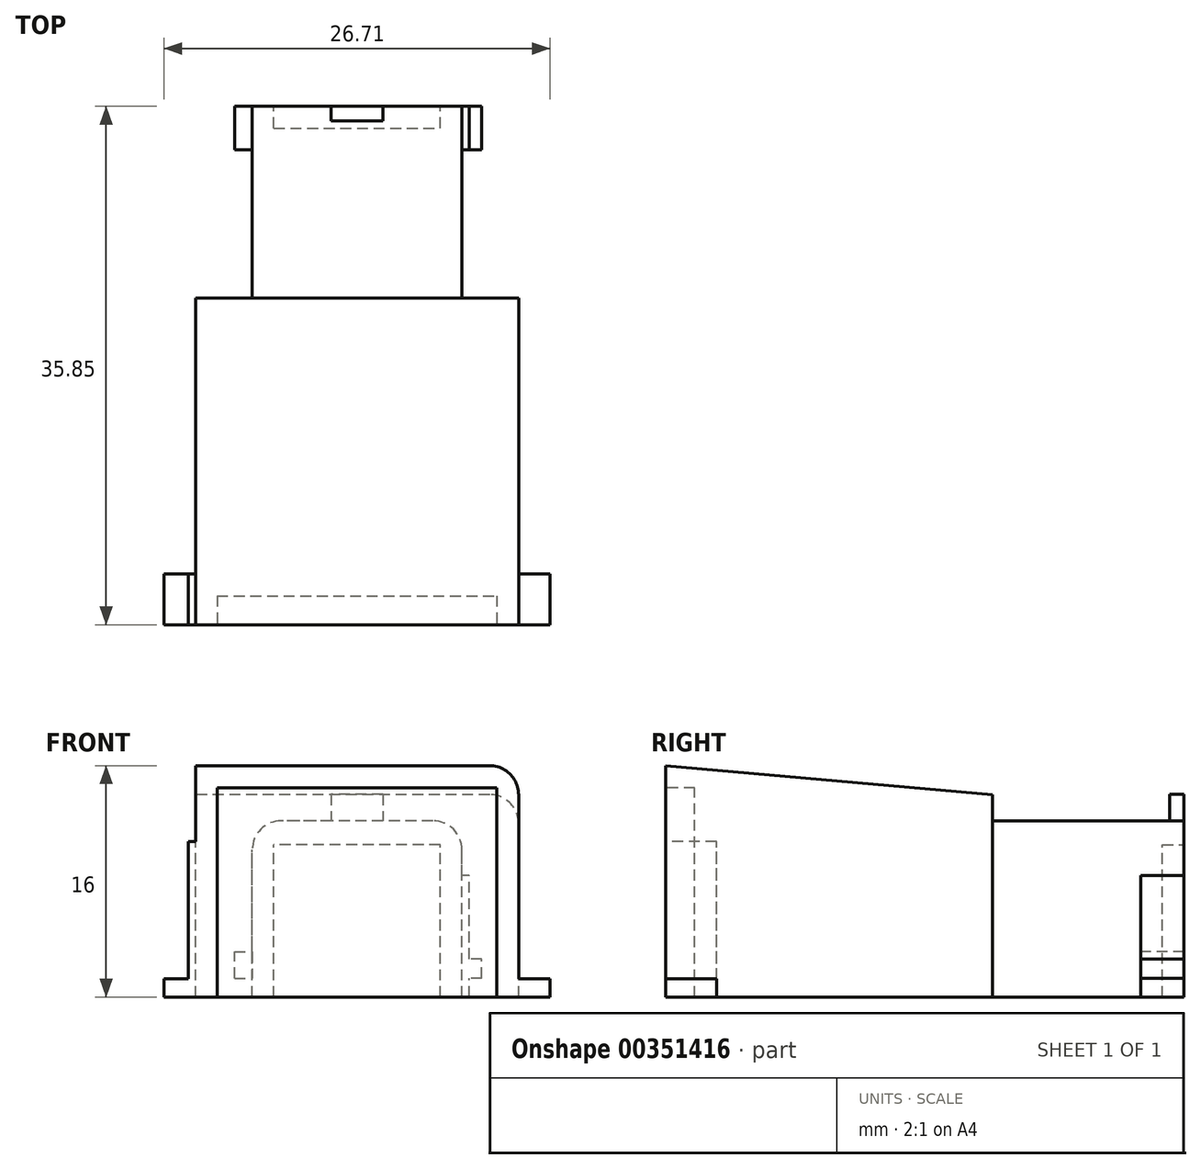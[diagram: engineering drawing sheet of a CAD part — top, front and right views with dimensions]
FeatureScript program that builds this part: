
annotation { "Feature Type Name" : "Feature", "Feature Type Description" : "" }
export const myFeature = defineFeature(function(context is Context, id is Id, definition is map)
    precondition{}
    {
        {
            var Q0;
            Q0=qCreatedBy(makeId("Front.planeOp"),FACE);
            var sketch = newSketch(context, id + "F0", { "sketchPlane" : qUnion([Q0])});
            skLineSegment(sketch, "E0.bottom", {"start": v(-13.6, 0) * mm, "end": v(8.76, 0) * mm});
            skLineSegment(sketch, "E0.top", {"start": v(-13.6, 16) * mm, "end": v(8.76, 16) * mm});
            skLineSegment(sketch, "E0.left", {"start": v(-13.6, 0) * mm, "end": v(-13.6, 16) * mm});
            skLineSegment(sketch, "E0.right", {"start": v(8.76, 0) * mm, "end": v(8.76, 16) * mm});
            skSolve(sketch);
        }
        {
            var Q0;
            Q0 = qSketchRegion(id + "F0", true);
            extrude(context, id + "F1", {"entities" : qUnion([Q0]), "depth" : 22.6 * mm});
        }
        {
            var Q0;
            Q0=makeQuery(id+"F1.opExtrude","CAP_FACE",FACE,{"disambiguationData":[OSD([sQuery(id+"F0.wireOp",EDGE,"E0.bottom"),sQuery(id+"F0.wireOp",EDGE,"E0.top"),sQuery(id+"F0.wireOp",EDGE,"E0.left"),sQuery(id+"F0.wireOp",EDGE,"E0.right")])],"isStart":false});
            var sketch = newSketch(context, id + "F2", { "sketchPlane" : qUnion([Q0])});
            skLineSegment(sketch, "E1.bottom", {"start": v(-12.1, 0) * mm, "end": v(7.26, 0) * mm});
            skLineSegment(sketch, "E1.top", {"start": v(-12.1, 14.48) * mm, "end": v(7.26, 14.48) * mm});
            skLineSegment(sketch, "E1.left", {"start": v(-12.1, 0) * mm, "end": v(-12.1, 14.48) * mm});
            skLineSegment(sketch, "E1.right", {"start": v(7.26, 0) * mm, "end": v(7.26, 14.48) * mm});
            skSolve(sketch);
        }
        {
            var Q0;
            Q0 = qSketchRegion(id + "F2", true);
            extrude(context, id + "F3", {"entities" : qUnion([Q0]), "operationType" : NewBodyOperationType.REMOVE, "oppositeDirection" : true, "depth" : 2 * mm});
        }
        {
            var Q0;
            Q0=makeQuery(id+"F1.opExtrude","SWEPT_FACE",FACE,{"disambiguationData":[OSD([sQuery(id+"F0.wireOp",EDGE,"E0.left")])]});
            var sketch = newSketch(context, id + "F4", { "sketchPlane" : qUnion([Q0])});
            skLineSegment(sketch, "E2", {"start": v(0, 0) * mm, "end": v(0, 14) * mm, "construction": true});
            skLineSegment(sketch, "E3", {"start": v(0, 14) * mm, "end": v(22.6, 16) * mm});
            skLineSegment(sketch, "E4", {"start": v(22.6, 16) * mm, "end": v(0, 16) * mm});
            skLineSegment(sketch, "E5", {"start": v(0, 16) * mm, "end": v(0, 14) * mm});
            skSolve(sketch);
        }
        {
            var Q0;
            Q0 = qSketchRegion(id + "F4", true);
            extrude(context, id + "F5", {"entities" : qUnion([Q0]), "operationType" : NewBodyOperationType.REMOVE, "oppositeDirection" : true, "depth" : 25 * mm});
        }
        {
            var Q0;
            Q0=makeQuery(id+"F1.opExtrude","SWEPT_FACE",FACE,{"disambiguationData":[OSD([sQuery(id+"F0.wireOp",EDGE,"E0.left")])]});
            var sketch = newSketch(context, id + "F6", { "sketchPlane" : qUnion([Q0])});
            skLineSegment(sketch, "E6.bottom", {"start": v(22.6, 0) * mm, "end": v(19.1, 0) * mm});
            skLineSegment(sketch, "E6.top", {"start": v(22.6, 1.25) * mm, "end": v(19.1, 1.25) * mm});
            skLineSegment(sketch, "E6.left", {"start": v(22.6, 0) * mm, "end": v(22.6, 1.25) * mm});
            skLineSegment(sketch, "E6.right", {"start": v(19.1, 0) * mm, "end": v(19.1, 1.25) * mm});
            skSolve(sketch);
        }
        {
            var Q0;
            Q0 = qSketchRegion(id + "F6", true);
            extrude(context, id + "F7", {"entities" : qUnion([Q0]), "operationType" : NewBodyOperationType.ADD, "depth" : 2.18 * mm});
        }
        {
            var Q0;
            Q0=makeQuery(id+"F1.opExtrude","SWEPT_FACE",FACE,{"disambiguationData":[OSD([sQuery(id+"F0.wireOp",EDGE,"E0.right")])]});
            var sketch = newSketch(context, id + "F8", { "sketchPlane" : qUnion([Q0])});
            skLineSegment(sketch, "E7.bottom", {"start": v(-22.6, 0) * mm, "end": v(-19.1, 0) * mm});
            skLineSegment(sketch, "E7.top", {"start": v(-22.6, 1.25) * mm, "end": v(-19.1, 1.25) * mm});
            skLineSegment(sketch, "E7.left", {"start": v(-22.6, 0) * mm, "end": v(-22.6, 1.25) * mm});
            skLineSegment(sketch, "E7.right", {"start": v(-19.1, 0) * mm, "end": v(-19.1, 1.25) * mm});
            skSolve(sketch);
        }
        {
            var Q0;
            Q0 = qSketchRegion(id + "F8", true);
            extrude(context, id + "F9", {"entities" : qUnion([Q0]), "operationType" : NewBodyOperationType.ADD, "depth" : 2.18 * mm});
        }
        {
            var Q0;
            Q0=makeQuery(id+"F1.opExtrude","SWEPT_FACE",FACE,{"disambiguationData":[OSD([sQuery(id+"F0.wireOp",EDGE,"E0.left")])]});
            var sketch = newSketch(context, id + "F10", { "sketchPlane" : qUnion([Q0])});
            skLineSegment(sketch, "E8.bottom", {"start": v(19.1, 0) * mm, "end": v(22.6, 0) * mm});
            skLineSegment(sketch, "E8.top", {"start": v(19.1, 10.75) * mm, "end": v(22.6, 10.75) * mm});
            skLineSegment(sketch, "E8.left", {"start": v(19.1, 0) * mm, "end": v(19.1, 10.75) * mm});
            skLineSegment(sketch, "E8.right", {"start": v(22.6, 0) * mm, "end": v(22.6, 10.75) * mm});
            skSolve(sketch);
        }
        {
            var Q0;
            Q0 = qSketchRegion(id + "F10", true);
            extrude(context, id + "F11", {"entities" : qUnion([Q0]), "operationType" : NewBodyOperationType.ADD, "depth" : .5 * mm});
        }
        {
            var Q0;
            Q0=makeQuery(id+"F1.opExtrude","CAP_FACE",FACE,{"disambiguationData":[OSD([sQuery(id+"F0.wireOp",EDGE,"E0.bottom"),sQuery(id+"F0.wireOp",EDGE,"E0.top"),sQuery(id+"F0.wireOp",EDGE,"E0.left"),sQuery(id+"F0.wireOp",EDGE,"E0.right")])],"isStart":true});
            var sketch = newSketch(context, id + "F12", { "sketchPlane" : qUnion([Q0])});
            skLineSegment(sketch, "E9.bottom", {"start": v(-4.83, 0) * mm, "end": v(9.67, 0) * mm});
            skLineSegment(sketch, "E9.top", {"start": v(-4.83, 12.18) * mm, "end": v(9.67, 12.18) * mm});
            skLineSegment(sketch, "E9.left", {"start": v(-4.83, 0) * mm, "end": v(-4.83, 12.18) * mm});
            skLineSegment(sketch, "E9.right", {"start": v(9.67, 0) * mm, "end": v(9.67, 12.18) * mm});
            skSolve(sketch);
        }
        {
            var Q0;
            Q0 = qSketchRegion(id + "F12", true);
            extrude(context, id + "F13", {"entities" : qUnion([Q0]), "operationType" : NewBodyOperationType.ADD, "depth" : 13.25 * mm});
        }
        {
            var Q0;
            Q0=makeQuery(id+"F13.opExtrude","CAP_FACE",FACE,{"disambiguationData":[OSD([sQuery(id+"F12.wireOp",EDGE,"E9.bottom"),sQuery(id+"F12.wireOp",EDGE,"E9.top"),sQuery(id+"F12.wireOp",EDGE,"E9.left"),sQuery(id+"F12.wireOp",EDGE,"E9.right")])],"isStart":false});
            var sketch = newSketch(context, id + "F14", { "sketchPlane" : qUnion([Q0])});
            skLineSegment(sketch, "E10.bottom", {"start": v(-3.33, 0) * mm, "end": v(8.17, 0) * mm});
            skLineSegment(sketch, "E10.top", {"start": v(-3.33, 10.53) * mm, "end": v(8.17, 10.53) * mm});
            skLineSegment(sketch, "E10.left", {"start": v(-3.33, 0) * mm, "end": v(-3.33, 10.53) * mm});
            skLineSegment(sketch, "E10.right", {"start": v(8.17, 0) * mm, "end": v(8.17, 10.53) * mm});
            skSolve(sketch);
        }
        {
            var Q0;
            Q0 = qSketchRegion(id + "F14", true);
            extrude(context, id + "F15", {"entities" : qUnion([Q0]), "operationType" : NewBodyOperationType.REMOVE, "oppositeDirection" : true, "depth" : 1.5 * mm});
        }
        {
            var Q0;
            Q0=makeQuery(id+"F13.opExtrude","SWEPT_FACE",FACE,{"disambiguationData":[OSD([sQuery(id+"F12.wireOp",EDGE,"E9.top")])]});
            var sketch = newSketch(context, id + "F16", { "sketchPlane" : qUnion([Q0])});
            skLineSegment(sketch, "E11", {"start": v(-2.42, 13.25) * mm, "end": v(-2.42, 4.4) * mm, "construction": true});
            skLineSegment(sketch, "E12.bottom", {"start": v(-0.63, 13.25) * mm, "end": v(-4.2, 13.25) * mm});
            skLineSegment(sketch, "E12.top", {"start": v(-0.63, 12.25) * mm, "end": v(-4.2, 12.25) * mm});
            skLineSegment(sketch, "E12.left", {"start": v(-0.63, 13.25) * mm, "end": v(-0.63, 12.25) * mm});
            skLineSegment(sketch, "E12.right", {"start": v(-4.2, 13.25) * mm, "end": v(-4.2, 12.25) * mm});
            skPoint(sketch, "E12.middle", {"position": v(-2.42, 12.75) * mm});
            skSolve(sketch);
        }
        {
            var Q0;
            Q0 = qSketchRegion(id + "F16", true);
            extrude(context, id + "F17", {"entities" : qUnion([Q0]), "operationType" : NewBodyOperationType.ADD, "depth" : 1.83 * mm});
        }
        {
            var Q0;
            Q0=makeQuery(id+"F13.opExtrude","SWEPT_FACE",FACE,{"disambiguationData":[OSD([sQuery(id+"F12.wireOp",EDGE,"E9.left")])]});
            var sketch = newSketch(context, id + "F18", { "sketchPlane" : qUnion([Q0])});
            skLineSegment(sketch, "E13.bottom", {"start": v(13.25, 0) * mm, "end": v(10.25, 0) * mm});
            skLineSegment(sketch, "E13.top", {"start": v(13.25, 8.4) * mm, "end": v(10.25, 8.4) * mm});
            skLineSegment(sketch, "E13.left", {"start": v(13.25, 0) * mm, "end": v(13.25, 8.4) * mm});
            skLineSegment(sketch, "E13.right", {"start": v(10.25, 0) * mm, "end": v(10.25, 8.4) * mm});
            skSolve(sketch);
        }
        {
            var Q0;
            Q0 = qSketchRegion(id + "F18", true);
            extrude(context, id + "F19", {"entities" : qUnion([Q0]), "operationType" : NewBodyOperationType.ADD, "depth" : .5 * mm});
        }
        {
            var Q0;
            Q0=makeQuery(id+"F19.opExtrude","CAP_FACE",FACE,{"disambiguationData":[OSD([sQuery(id+"F18.wireOp",EDGE,"E13.bottom"),sQuery(id+"F18.wireOp",EDGE,"E13.top"),sQuery(id+"F18.wireOp",EDGE,"E13.left"),sQuery(id+"F18.wireOp",EDGE,"E13.right")])],"isStart":false});
            var sketch = newSketch(context, id + "F20", { "sketchPlane" : qUnion([Q0])});
            skLineSegment(sketch, "E14.bottom", {"start": v(10.25, 1.3) * mm, "end": v(13.25, 1.3) * mm});
            skLineSegment(sketch, "E14.top", {"start": v(10.25, 2.62) * mm, "end": v(13.25, 2.62) * mm});
            skLineSegment(sketch, "E14.left", {"start": v(10.25, 1.3) * mm, "end": v(10.25, 2.62) * mm});
            skLineSegment(sketch, "E14.right", {"start": v(13.25, 1.3) * mm, "end": v(13.25, 2.62) * mm});
            skSolve(sketch);
        }
        {
            var Q0;
            Q0 = qSketchRegion(id + "F20", true);
            extrude(context, id + "F21", {"entities" : qUnion([Q0]), "operationType" : NewBodyOperationType.ADD, "depth" : .88 * mm});
        }
        {
            var Q0;
            Q0=makeQuery(id+"F13.opExtrude","SWEPT_FACE",FACE,{"disambiguationData":[OSD([sQuery(id+"F12.wireOp",EDGE,"E9.right")])]});
            var sketch = newSketch(context, id + "F22", { "sketchPlane" : qUnion([Q0])});
            skLineSegment(sketch, "E15.bottom", {"start": v(-13.25, 3.12) * mm, "end": v(-10.25, 3.12) * mm});
            skLineSegment(sketch, "E15.top", {"start": v(-13.25, 1.3) * mm, "end": v(-10.25, 1.3) * mm});
            skLineSegment(sketch, "E15.left", {"start": v(-13.25, 3.12) * mm, "end": v(-13.25, 1.3) * mm});
            skLineSegment(sketch, "E15.right", {"start": v(-10.25, 3.12) * mm, "end": v(-10.25, 1.3) * mm});
            skSolve(sketch);
        }
        {
            var Q0;
            Q0 = qSketchRegion(id + "F22", true);
            extrude(context, id + "F23", {"entities" : qUnion([Q0]), "operationType" : NewBodyOperationType.ADD, "depth" : 1.23 * mm});
        }
        {
            var Q0;
            Q0=makeQuery(id+"F5.boolean.opBoolean","COPY",EDGE,{"derivedFrom":makeQuery(id+"F5.opExtrude","CAP_EDGE",EDGE,{"disambiguationData":[OSD([sQuery(id+"F4.wireOp",EDGE,"E3")])],"isStart":true})});
            var Q1;
            Q1=makeQuery(id+"F5.boolean.opBoolean","INTERSECT",EDGE,{"derivedFrom":[makeQuery(id+"F1.opExtrude","SWEPT_FACE",FACE,{"disambiguationData":[OSD([sQuery(id+"F0.wireOp",EDGE,"E0.right")])]}),makeQuery(id+"F5.opExtrude","SWEPT_FACE",FACE,{"disambiguationData":[OSD([sQuery(id+"F4.wireOp",EDGE,"E3")])]})]});
            var Q2;
            Q2=makeQuery(id+"F13.opExtrude","SWEPT_EDGE",EDGE,{"disambiguationData":[OSD([sQuery(id+"F12.wireOp",EDGE,"E9.top"),sQuery(id+"F12.wireOp",EDGE,"E9.left")])]});
            var Q3;
            Q3=makeQuery(id+"F13.opExtrude","SWEPT_EDGE",EDGE,{"disambiguationData":[OSD([sQuery(id+"F12.wireOp",EDGE,"E9.top"),sQuery(id+"F12.wireOp",EDGE,"E9.right")])]});
            fillet(context, id + "F24", {"entities" : qUnion([Q0, Q1, Q2, Q3]), "radius" : 2 * mm, "tangentPropagation" : true, "allowEdgeOverflow" : false});
        }
    });
